# Revit family: Electronics_Desono_Biamp_Compact-Column-Point-Source-Loudspeaker_ENT220
name_source: partatom
category: Communication Devices
units: mm (PartAtom-declared; Revit-internal decimal feet)

## family parameters
Cut with Voids When Loaded = No
Host = Face
Maintain Annotation Orientation = No
OmniClass Number = 23.85.10.11.14.14.14
Part Type = Normal
Room Calculation Point = No
Round Connector Dimension = Use Diameter
Shared = No

## types (2) — shared parameters
Autoformer = 70 V - 120 W,60 W,30 W,15W,7.5 W;100 V - 120 W,60 W,30 W,15 W
Connector Description = Terminal strip; Low impedance 8 ohms, 70/100V operation
Continuous Power Handling Nominal Impedance = Passive; 63V; 500W @ 8Ω (2000W peak)
Default Elevation = 48 "
Depth = 7 "
Description = Desono™ ENT220 Two-Way, Compact Column Point Source Loudspeaker
Environmental = IP54 per IEC 60529, designed in accordance with MIL-STD-810G Included ABS plastic rain cover with integrated cable inlet and 1 (25.4mm) knockout for conduit ingress
Equalized Maximum SPL = System: Peak - 132dB; Continuous - 126dB
Equalized Sensitivity = Sustem: 1W - 99dB; 2.83V - 99dB
Height_2 = 65 "
Input Connection = NL4-type connector for low impedance operation, and 8-position terminal strip for low impedance or constant voltage operation
Manufacturer = Biamp
Mounting Points = Small pan-tilt mounting bracket included;(up to 10.8° down-tilt, ± 55° panning)
Nominal Beamwidth  (H x V) = 140° x  15°
Nominal Maximum SPL (Whole Space) = Passive: Peak - 132dB; Continuous - 126dB
Nominal Sensitivity = Passive: 1W - 99dB; 2.83V - 99dB
Operating Environment = Indoor or outdoor
Operating Mode = Passive
Operating Range = 80 Hz to 22 kHz
Product Documentation Link = https://downloads.biamp.com
Product Page URL = https://www.biamp.com
Product data url = https://www.bimobject.com
Recommended Amplifers = Passive - 500 W - 1000 W @ 8 Ω (63 V - 89 V)
Required Accessories = External High Pass Filter - 80 Hz, 24 dB /octave Digital Signal Processor
Shipping Weight = 60.00 lb
Transducers = LF   20 x 80mm long excursion mylar driver HF  4 x 3-element Compact Ribbon Emulator
URL = https://www.biamp.com
Weight = 41.00 lb
Width = 5 "

## per-type parameters (varying)
| type | Bracket Material | Grill Material | Housing Material |
| ENT220 W | Biamp - Metal - White | Biamp - Plastic - White(Grid) | Biamp - Plastic - White |
| ENT220 B | Biamp - Metal - Black | Biamp - Plastic - Black(Grid) | Biamp - Plastic - Black |

note: column(s) folded — value = type name in every type: Model

## geometry (parser evidence)
native form markers: Sweep x9
no freeform markers — native parametric forms only
